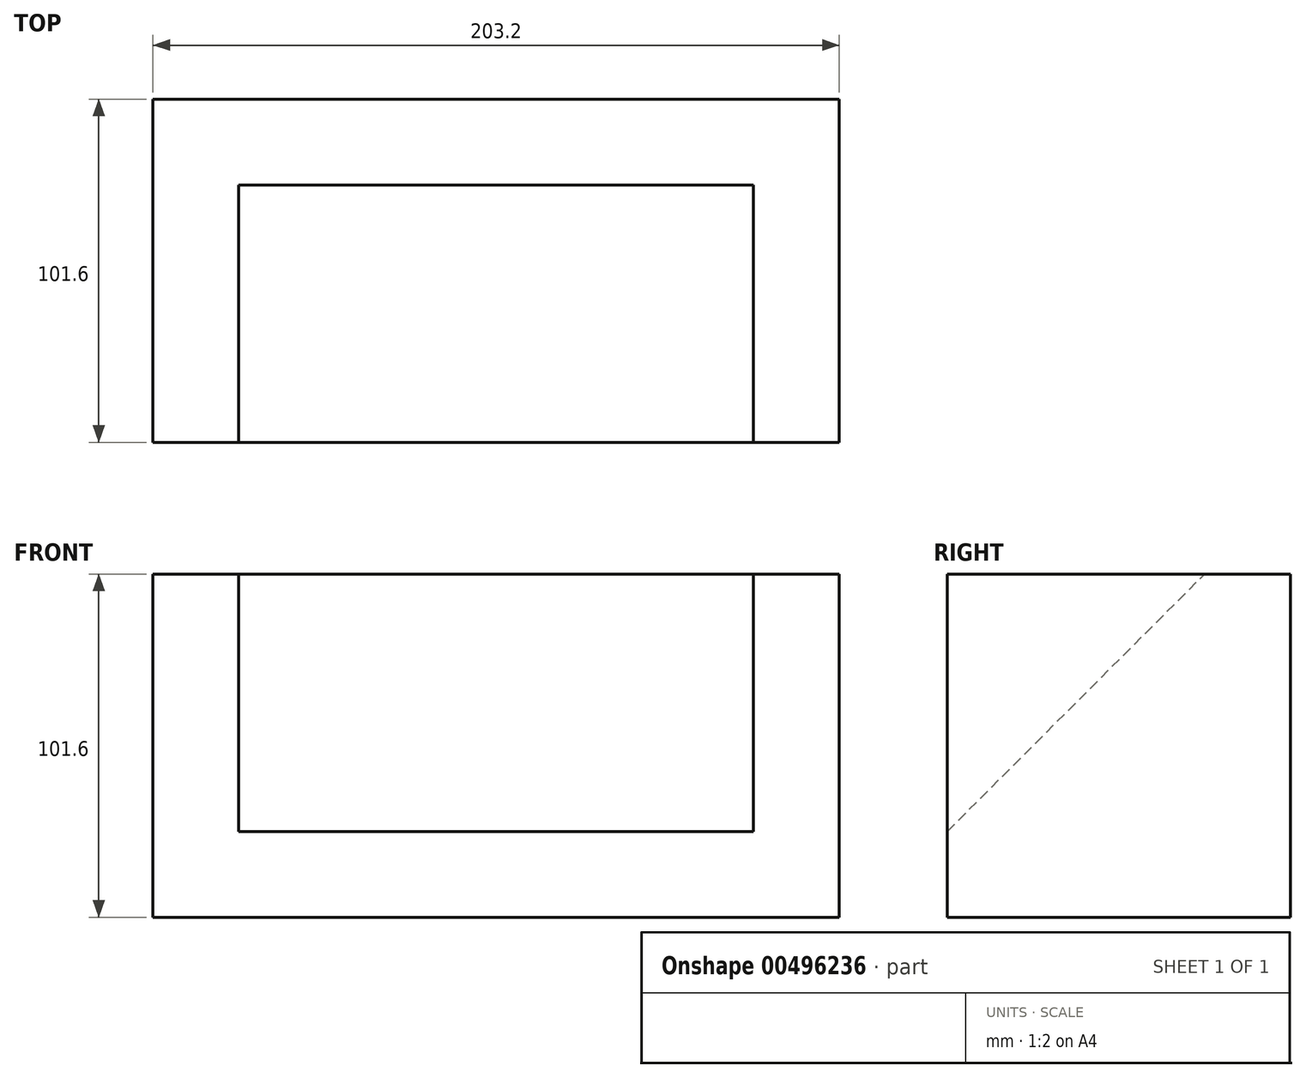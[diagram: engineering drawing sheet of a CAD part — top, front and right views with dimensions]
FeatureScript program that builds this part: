
annotation { "Feature Type Name" : "Feature", "Feature Type Description" : "" }
export const myFeature = defineFeature(function(context is Context, id is Id, definition is map)
    precondition{}
    {
        {
            var Q0;
            Q0=qCreatedBy(makeId("Front.planeOp"),FACE);
            var sketch = newSketch(context, id + "F0", { "sketchPlane" : qUnion([Q0])});
            skLineSegment(sketch, "E0.bottom", {"start": v(0, 0) * mm, "end": v(101.6, 0) * mm});
            skLineSegment(sketch, "E0.top", {"start": v(0, 101.6) * mm, "end": v(101.6, 101.6) * mm});
            skLineSegment(sketch, "E0.left", {"start": v(0, 0) * mm, "end": v(0, 101.6) * mm});
            skLineSegment(sketch, "E0.right", {"start": v(101.6, 0) * mm, "end": v(101.6, 101.6) * mm});
            skSolve(sketch);
        }
        {
            var Q0;
            Q0=makeQuery(id+"F0.imprint","IMPRINT",FACE,{"disambiguationData":[TD([[makeQuery(id+"F0.imprint","IMPRINT",EDGE,{"derivedFrom":sQuery(id+"F0.wireOp",EDGE,"E0.bottom")}),1.0]])]});
            var sketch = newSketch(context, id + "F1", { "sketchPlane" : qUnion([Q0])});
            skLineSegment(sketch, "E1", {"start": v(0, 0) * mm, "end": v(0, 25.4) * mm});
            skLineSegment(sketch, "E2.bottom", {"start": v(0, 25.4) * mm, "end": v(76.2, 25.4) * mm});
            skLineSegment(sketch, "E2.top", {"start": v(0, 101.6) * mm, "end": v(76.2, 101.6) * mm});
            skLineSegment(sketch, "E2.left", {"start": v(0, 25.4) * mm, "end": v(0, 101.6) * mm});
            skLineSegment(sketch, "E2.right", {"start": v(76.2, 25.4) * mm, "end": v(76.2, 101.6) * mm});
            skLineSegment(sketch, "E3", {"start": v(0, 25.4) * mm, "end": v(76.2, 101.6) * mm});
            skSolve(sketch);
        }
        {
            var Q0;
            Q0=makeQuery(id+"F0.imprint","IMPRINT",FACE,{"disambiguationData":[TD([[makeQuery(id+"F0.imprint","IMPRINT",EDGE,{"derivedFrom":sQuery(id+"F0.wireOp",EDGE,"E0.bottom")}),1.0]])]});
            extrude(context, id + "F2", {"entities" : qUnion([Q0]), "depth" : 203.2 * mm});
        }
        {
            var Q0;
            Q0=makeQuery(id+"F1.imprint","IMPRINT",FACE,{"disambiguationData":[TD([[makeQuery(id+"F1.imprint","IMPRINT",EDGE,{"derivedFrom":sQuery(id+"F1.wireOp",EDGE,"E2.top")}),-1.0]])]});
            extrude(context, id + "F3", {"entities" : qUnion([Q0]), "operationType" : NewBodyOperationType.REMOVE, "depth" : 203.2 * mm});
        }
        {
            var Q0;
            Q0=qCreatedBy(makeId("Front.planeOp"),FACE);
            var sketch = newSketch(context, id + "F4", { "sketchPlane" : qUnion([Q0])});
            skLineSegment(sketch, "E4.bottom", {"start": v(0, 0) * mm, "end": v(101.6, 0) * mm});
            skLineSegment(sketch, "E4.top", {"start": v(0, 101.6) * mm, "end": v(101.6, 101.6) * mm});
            skLineSegment(sketch, "E4.left", {"start": v(0, 0) * mm, "end": v(0, 101.6) * mm});
            skLineSegment(sketch, "E4.right", {"start": v(101.6, 0) * mm, "end": v(101.6, 101.6) * mm});
            skSolve(sketch);
        }
        {
            var Q0;
            Q0 = qSketchRegion(id + "F4", true);
            extrude(context, id + "F5", {"entities" : qUnion([Q0]), "operationType" : NewBodyOperationType.ADD, "depth" : 25.4 * mm});
        }
        {
            var Q0;
            Q0=makeQuery(id+"F2.opExtrude","CAP_FACE",FACE,{"disambiguationData":[OSD([sQuery(id+"F0.wireOp",EDGE,"E0.bottom"),sQuery(id+"F0.wireOp",EDGE,"E0.top"),sQuery(id+"F0.wireOp",EDGE,"E0.left"),sQuery(id+"F0.wireOp",EDGE,"E0.right")])],"isStart":false});
            var sketch = newSketch(context, id + "F6", { "sketchPlane" : qUnion([Q0])});
            skLineSegment(sketch, "E5.bottom", {"start": v(0, 0) * mm, "end": v(101.6, 0) * mm});
            skLineSegment(sketch, "E5.top", {"start": v(0, 101.6) * mm, "end": v(101.6, 101.6) * mm});
            skLineSegment(sketch, "E5.left", {"start": v(0, 0) * mm, "end": v(0, 101.6) * mm});
            skLineSegment(sketch, "E5.right", {"start": v(101.6, 0) * mm, "end": v(101.6, 101.6) * mm});
            skSolve(sketch);
        }
        {
            var Q0;
            Q0 = qSketchRegion(id + "F6", true);
            extrude(context, id + "F7", {"entities" : qUnion([Q0]), "operationType" : NewBodyOperationType.ADD, "oppositeDirection" : true, "depth" : 25.4 * mm});
        }
        {
            var Q0;
            Q0=makeQuery(id+"F2.opExtrude","SWEPT_BODY",BODY,{"disambiguationData":[OSD([sQuery(id+"F0.wireOp",EDGE,"E0.bottom"),sQuery(id+"F0.wireOp",EDGE,"E0.top"),sQuery(id+"F0.wireOp",EDGE,"E0.left"),sQuery(id+"F0.wireOp",EDGE,"E0.right")])]});
            var Q1;
            Q1=makeQuery(id+"F2.opExtrude","CAP_EDGE",EDGE,{"disambiguationData":[OSD([sQuery(id+"F0.wireOp",EDGE,"E0.right")])],"isStart":false});
            transform(context, id + "F8", {"entities" : qUnion([Q0]), "transformType" : TransformType.ROTATION, "transformAxis" : qUnion([Q1]), "angle" : 90 * degree, "makeCopy" : false});
        }
    });
